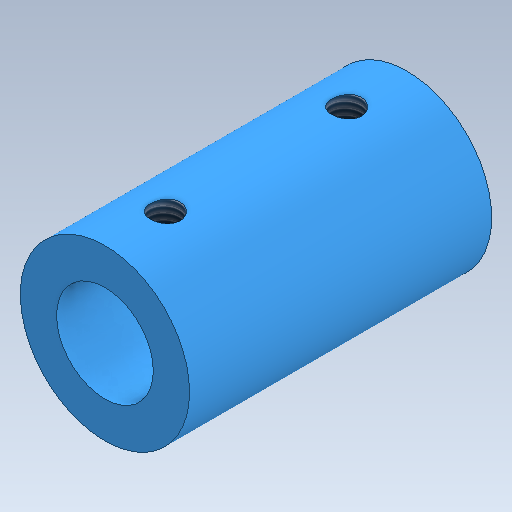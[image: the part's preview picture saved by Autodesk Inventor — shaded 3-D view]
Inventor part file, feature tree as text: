
AUTODESK INVENTOR PART (.ipt)
format: ipt  version: 2020 (Build 240168000, 168)  size: 142,848 bytes
history: native  units: mm
features: sketch x3, hole x2, extrude x1
ambient origin geometry x8: Origin, YZ Plane, XZ Plane, XY Plane, X Axis, Y Axis, Z Axis, Center Point
bodies: Solid1 (feature_tree)
feature tree (6):
  extrude  "Extrusion1"  Depth=25.0mm TaperAngle=0.0deg
  hole  "Hole1"  [1 undecoded]
  hole  "Hole2"  [1 undecoded]
  sketch  "Sketch1"  dims[d0=14.0mm d1=25.0mm d2=0.0mm]
  sketch  "Sketch3"  dims[d3=5.0mm d4=6.0mm d5=8.0mm d6=12.5mm d7=90.0deg d8=8.0mm d9=20.594885mm d10=5.0mm]
  sketch  "Sketch4"  dims[d11=5.0mm d12=2.459mm d13=8.0mm d14=8.0mm d15=12.5mm d16=90.0deg d17=8.8mm d18=20.594885mm]
note: 2 required parameter values undecoded (feature->parameter linkage not recoverable at this tier; creation-order binding heuristic only, values carry confidence <= 0.55)
